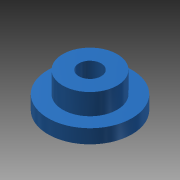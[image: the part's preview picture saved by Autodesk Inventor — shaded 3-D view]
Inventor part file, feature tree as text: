
AUTODESK INVENTOR PART (.ipt)
format: ipt  version: 2013 (Build 170138000, 138)  size: 87,040 bytes
history: native  units: mm
features: extrude x2, sketch x2
ambient origin geometry x8: Origin, YZ Plane, XZ Plane, XY Plane, X Axis, Y Axis, Z Axis, Center Point
bodies: Solid1 (feature_tree)
feature tree (4):
  extrude  "Extrusion1"  Depth=12.0mm
  extrude  "Extrusion2"  Depth=7.8mm
  sketch  "Sketch1"  dims[d0=3.2mm d1=12.0mm]
  sketch  "Sketch2"  dims[d2=2.0mm d3=0.0mm d4=7.8mm d5=3.0mm d6=0.0mm]
